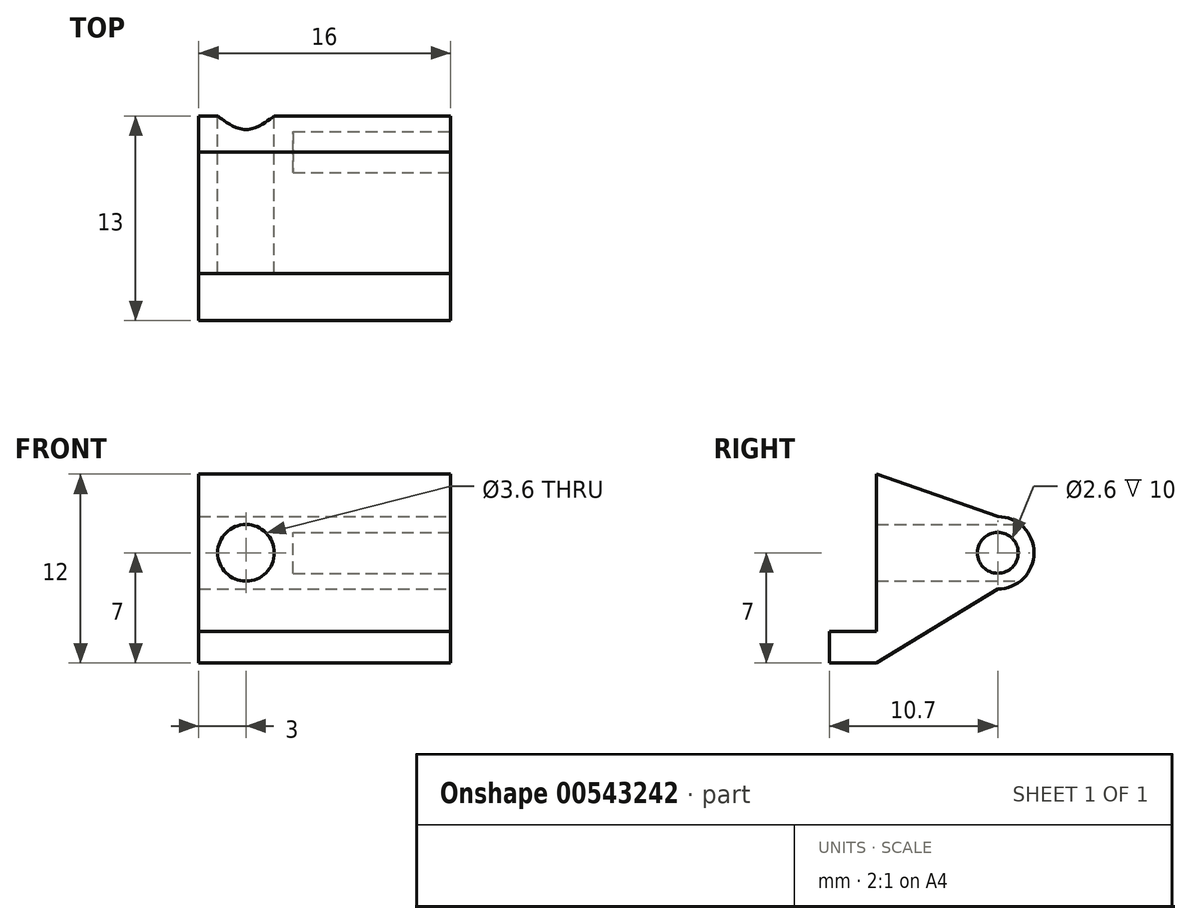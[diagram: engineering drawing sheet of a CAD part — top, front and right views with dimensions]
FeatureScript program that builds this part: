
annotation { "Feature Type Name" : "Feature", "Feature Type Description" : "" }
export const myFeature = defineFeature(function(context is Context, id is Id, definition is map)
    precondition{}
    {
        {
            var Q0;
            Q0=qCreatedBy(makeId("Front.planeOp"),FACE);
            var sketch = newSketch(context, id + "F0", { "sketchPlane" : qUnion([Q0])});
            skLineSegment(sketch, "E0.bottom", {"start": v(-13.34, 5) * mm, "end": v(2.66, 5) * mm});
            skLineSegment(sketch, "E0.top", {"start": v(-13.34, -7) * mm, "end": v(2.66, -7) * mm});
            skLineSegment(sketch, "E0.left", {"start": v(-13.34, 5) * mm, "end": v(-13.34, -7) * mm});
            skLineSegment(sketch, "E0.right", {"start": v(2.66, 5) * mm, "end": v(2.66, -7) * mm});
            skCircle(sketch, "E1", {"center": v(-10.34, 0) * mm, "radius": 1.8 * mm});
            skSolve(sketch);
        }
        {
            var Q0;
            Q0=makeQuery(id+"F0.imprint","IMPRINT",FACE,{"disambiguationData":[TD([[makeQuery(id+"F0.imprint","IMPRINT",EDGE,{"derivedFrom":sQuery(id+"F0.wireOp",EDGE,"E0.bottom")}),-1.0]])]});
            extrude(context, id + "F1", {"entities" : qUnion([Q0]), "depth" : 13 * mm, "offsetDistance" : 25 * mm});
        }
        {
            var Q0;
            Q0=makeQuery(id+"F1.opExtrude","CAP_FACE",FACE,{"disambiguationData":[OSD([sQuery(id+"F0.wireOp",EDGE,"E0.bottom"),sQuery(id+"F0.wireOp",EDGE,"E0.top"),sQuery(id+"F0.wireOp",EDGE,"E0.left"),sQuery(id+"F0.wireOp",EDGE,"E0.right"),sQuery(id+"F0.wireOp",EDGE,"E1")])],"isStart":false});
            var sketch = newSketch(context, id + "F2", { "sketchPlane" : qUnion([Q0])});
            skLineSegment(sketch, "E2", {"start": v(2.66, -5) * mm, "end": v(-13.34, -5) * mm});
            skSolve(sketch);
        }
        {
            var Q0;
            {var subQ2=sQuery(id+"F2.wireOp",EDGE,"E2");Q0=makeQuery(id+"F2.imprint","IMPRINT",FACE,{"disambiguationData":[TD([[makeQuery(id+"F2.imprint","IMPRINT",EDGE,{"derivedFrom":subQ2}),-1.0]])]});}
            extrude(context, id + "F3", {"entities" : qUnion([Q0]), "operationType" : NewBodyOperationType.REMOVE, "oppositeDirection" : true, "depth" : 3 * mm, "offsetDistance" : 25 * mm});
        }
        {
            var Q0;
            Q0=makeQuery(id+"F1.opExtrude","SWEPT_FACE",FACE,{"disambiguationData":[OSD([sQuery(id+"F0.wireOp",EDGE,"E0.right")])]});
            var sketch = newSketch(context, id + "F4", { "sketchPlane" : qUnion([Q0])});
            skCircle(sketch, "E3", {"center": v(-2.3, 0) * mm, "radius": 2.3 * mm});
            skLineSegment(sketch, "E4", {"start": v(-2.3, 2.3) * mm, "end": v(-10, 5) * mm});
            skPoint(sketch, "E5.start.orphan", {"position": v(-2.3, -2.3) * mm});
            skLineSegment(sketch, "E6", {"start": v(-2.3, -2.3) * mm, "end": v(-10, -7) * mm});
            skSolve(sketch);
        }
        {
            var Q0;
            {var subQ0=sQuery(id+"F4.wireOp",EDGE,"E4");Q0=makeQuery(id+"F4.imprint","IMPRINT",FACE,{"disambiguationData":[TD([[makeQuery(id+"F4.imprint","IMPRINT",EDGE,{"derivedFrom":subQ0}),-1.0]])]});}
            var Q1;
            {var subQ0=sQuery(id+"F4.wireOp",EDGE,"E5");Q1=makeQuery(id+"F4.imprint","IMPRINT",FACE,{"disambiguationData":[TD([[makeQuery(id+"F4.imprint","IMPRINT",EDGE,{"derivedFrom":subQ0}),1.0]])]});}
            var Q2;
            {var subQ0=sQuery(id+"F4.wireOp",EDGE,"E6");Q2=makeQuery(id+"F4.imprint","IMPRINT",FACE,{"disambiguationData":[TD([[makeQuery(id+"F4.imprint","IMPRINT",EDGE,{"derivedFrom":subQ0}),1.0]])]});}
            extrude(context, id + "F5", {"entities" : qUnion([Q0, Q1, Q2]), "operationType" : NewBodyOperationType.REMOVE, "endBound" : BoundingType.THROUGH_ALL, "oppositeDirection" : true, "depth" : 25 * mm, "offsetDistance" : 25 * mm});
        }
        {
            var Q0;
            Q0=makeQuery(id+"F1.opExtrude","SWEPT_FACE",FACE,{"disambiguationData":[OSD([sQuery(id+"F0.wireOp",EDGE,"E0.right")])]});
            var sketch = newSketch(context, id + "F6", { "sketchPlane" : qUnion([Q0])});
            skCircle(sketch, "E7", {"center": v(-2.3, 0) * mm, "radius": 1.3 * mm});
            skSolve(sketch);
        }
        {
            var Q0;
            Q0=makeQuery(id+"F6.imprint","IMPRINT",FACE,{"disambiguationData":[TD([[makeQuery(id+"F6.imprint","IMPRINT",EDGE,{"derivedFrom":sQuery(id+"F6.wireOp",EDGE,"E7")}),1.0]])]});
            extrude(context, id + "F7", {"entities" : qUnion([Q0]), "operationType" : NewBodyOperationType.REMOVE, "oppositeDirection" : true, "depth" : 10 * mm, "offsetDistance" : 25 * mm});
        }
    });
